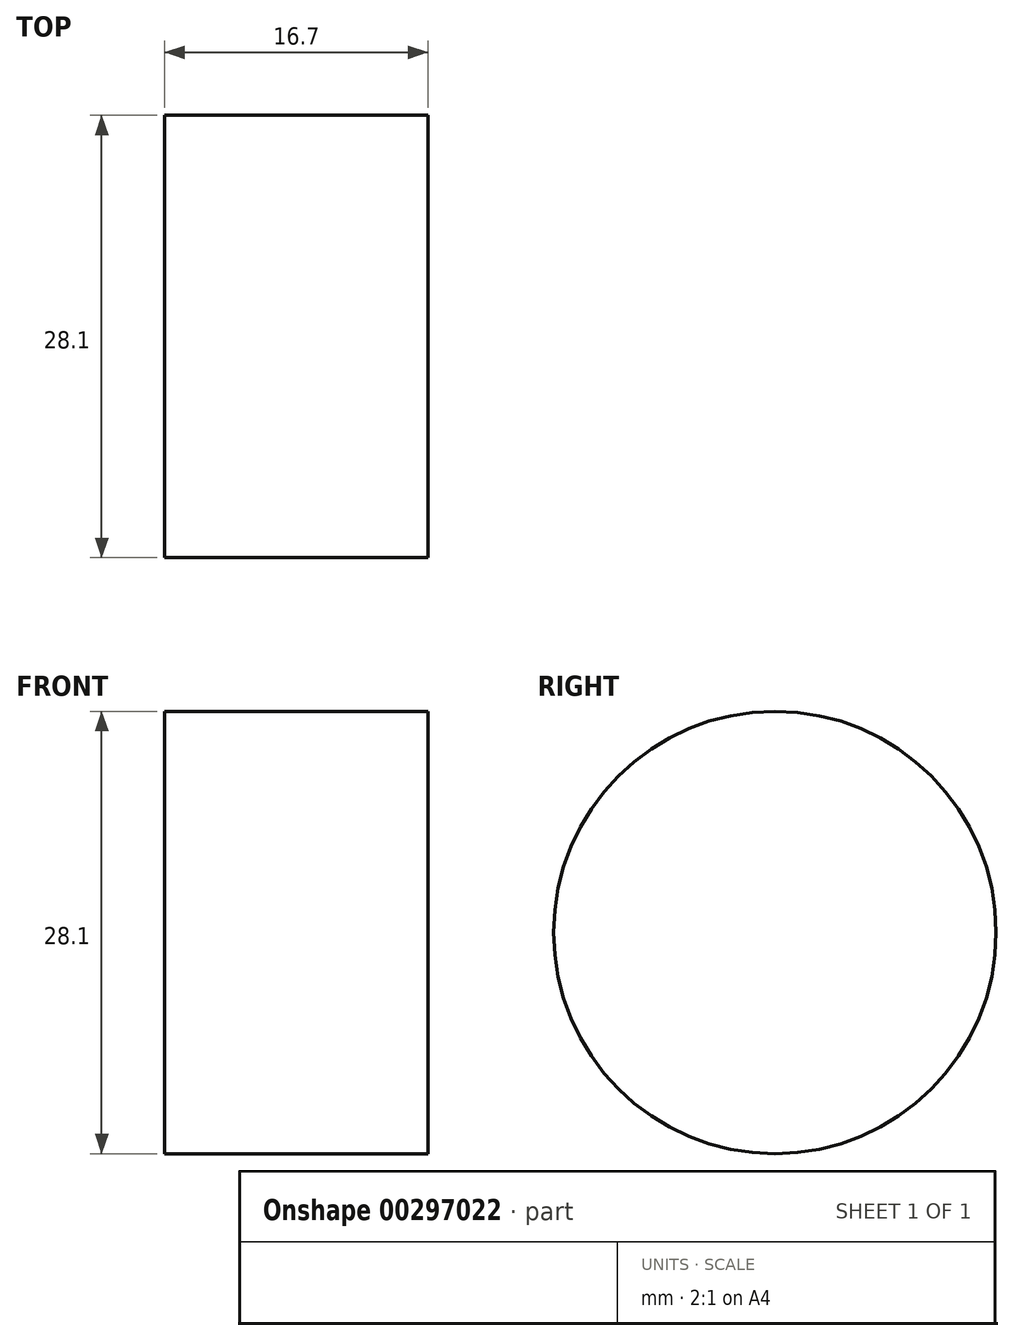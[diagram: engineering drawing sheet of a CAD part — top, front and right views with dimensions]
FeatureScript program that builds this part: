
annotation { "Feature Type Name" : "Feature", "Feature Type Description" : "" }
export const myFeature = defineFeature(function(context is Context, id is Id, definition is map)
    precondition{}
    {
        {
            var Q0;
            Q0=qCreatedBy(makeId("Front.planeOp"),FACE);
            var sketch = newSketch(context, id + "F0", { "sketchPlane" : qUnion([Q0])});
            skLineSegment(sketch, "E0.bottom", {"start": v(-16.7, 14.05) * mm, "end": v(0, 14.05) * mm});
            skLineSegment(sketch, "E0.top", {"start": v(-16.7, -14.05) * mm, "end": v(0, -14.05) * mm});
            skLineSegment(sketch, "E0.left", {"start": v(-16.7, 14.05) * mm, "end": v(-16.7, -14.05) * mm});
            skLineSegment(sketch, "E0.right", {"start": v(0, 14.05) * mm, "end": v(0, -14.05) * mm});
            skLineSegment(sketch, "E1.bottom", {"start": v(-16.7, -11.5) * mm, "end": v(-16.7, -11.5) * mm});
            skLineSegment(sketch, "E1.top", {"start": v(-16.7, 11.5) * mm, "end": v(-16.7, 11.5) * mm});
            skLineSegment(sketch, "E1.left", {"start": v(-16.7, 11.5) * mm, "end": v(-16.7, -11.5) * mm});
            skLineSegment(sketch, "E1.right", {"start": v(-16.7, 11.5) * mm, "end": v(-16.7, -11.5) * mm});
            skLineSegment(sketch, "E2", {"start": v(0, 0) * mm, "end": v(-16.7, 0) * mm});
            skSolve(sketch);
        }
        {
            var Q0;
            {var subQ5=sQuery(id+"F0.wireOp",EDGE,"E0.bottom");Q0=makeQuery(id+"F0.imprint","IMPRINT",FACE,{"disambiguationData":[TD([[makeQuery(id+"F0.imprint","IMPRINT",EDGE,{"derivedFrom":subQ5}),-1.0]])]});}
            var Q1;
            Q1=sQuery(id+"F0.wireOp",EDGE,"E2");
            revolve(context, id + "F1", {"entities" : qUnion([Q0]), "axis" : qUnion([Q1]), "revolveType" : RevolveType.FULL});
        }
    });
